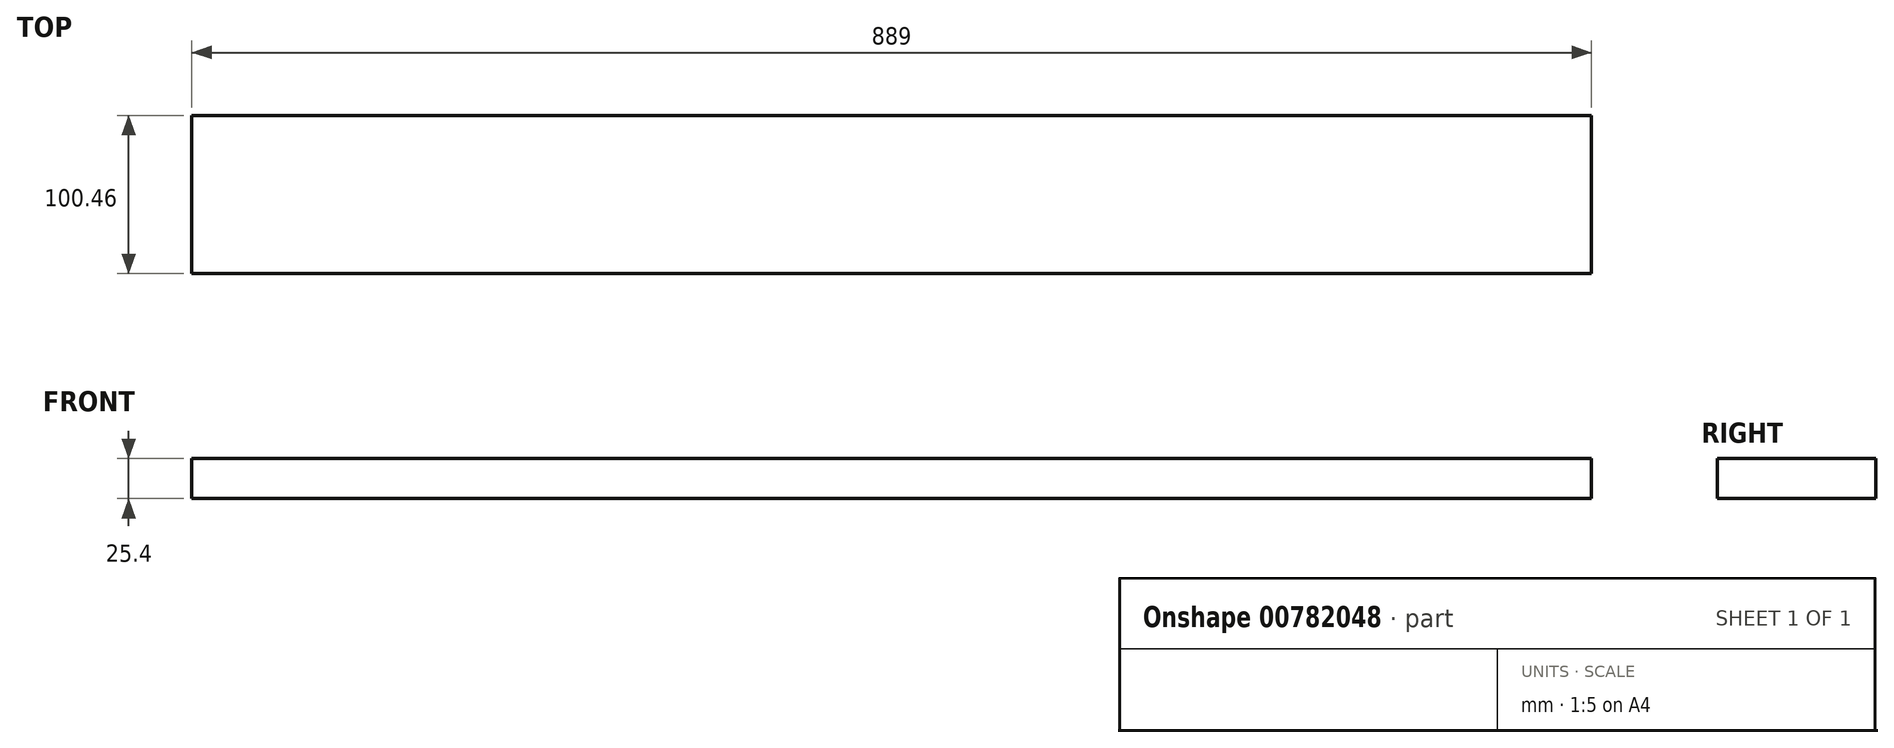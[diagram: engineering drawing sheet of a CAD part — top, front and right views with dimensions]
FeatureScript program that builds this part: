
annotation { "Feature Type Name" : "Feature", "Feature Type Description" : "" }
export const myFeature = defineFeature(function(context is Context, id is Id, definition is map)
    precondition{}
    {
        {
            var Q0;
            Q0=qCreatedBy(makeId("Top.planeOp"),FACE);
            var sketch = newSketch(context, id + "F0", { "sketchPlane" : qUnion([Q0])});
            skLineSegment(sketch, "E0.bottom", {"start": v(444.5, 50.23) * mm, "end": v(-444.5, 50.23) * mm});
            skLineSegment(sketch, "E0.top", {"start": v(444.5, -50.23) * mm, "end": v(-444.5, -50.23) * mm});
            skLineSegment(sketch, "E0.left", {"start": v(444.5, 50.23) * mm, "end": v(444.5, -50.23) * mm});
            skLineSegment(sketch, "E0.right", {"start": v(-444.5, 50.23) * mm, "end": v(-444.5, -50.23) * mm});
            skPoint(sketch, "E0.middle", {"position": v(0, 0) * mm});
            skSolve(sketch);
        }
        {
            var Q0;
            Q0=makeQuery(id+"F0.imprint","IMPRINT",FACE,{"disambiguationData":[TD([[makeQuery(id+"F0.imprint","IMPRINT",EDGE,{"derivedFrom":sQuery(id+"F0.wireOp",EDGE,"E0.bottom")}),1.0]])]});
            extrude(context, id + "F1", {"entities" : qUnion([Q0]), "depth" : 25.4 * mm, "offsetDistance" : 25.4 * mm});
        }
    });
